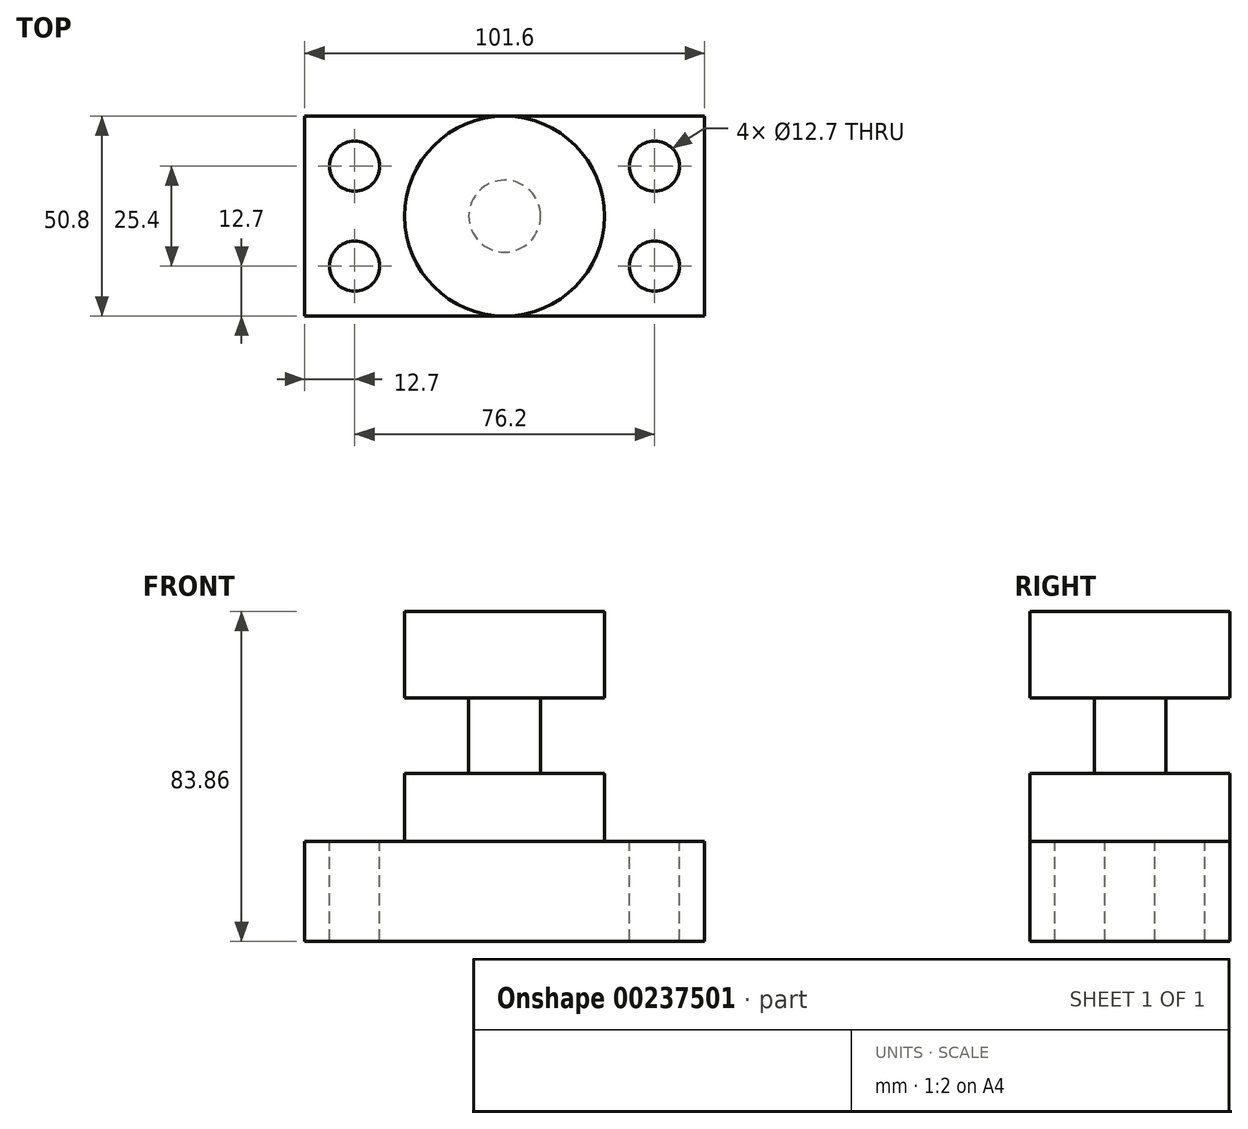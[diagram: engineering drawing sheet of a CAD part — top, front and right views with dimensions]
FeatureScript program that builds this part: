
annotation { "Feature Type Name" : "Feature", "Feature Type Description" : "" }
export const myFeature = defineFeature(function(context is Context, id is Id, definition is map)
    precondition{}
    {
        {
            var Q0;
            Q0=qCreatedBy(makeId("Top.planeOp"),FACE);
            var sketch = newSketch(context, id + "F0", { "sketchPlane" : qUnion([Q0])});
            skLineSegment(sketch, "E0.bottom", {"start": v(-50.8, 25.4) * mm, "end": v(50.8, 25.4) * mm});
            skLineSegment(sketch, "E0.top", {"start": v(-50.8, -25.4) * mm, "end": v(50.8, -25.4) * mm});
            skLineSegment(sketch, "E0.left", {"start": v(-50.8, 25.4) * mm, "end": v(-50.8, -25.4) * mm});
            skLineSegment(sketch, "E0.right", {"start": v(50.8, 25.4) * mm, "end": v(50.8, -25.4) * mm});
            skPoint(sketch, "E0.middle", {"position": v(0, 0) * mm});
            skSolve(sketch);
        }
        {
            var Q0;
            Q0=makeQuery(id+"F0.imprint","IMPRINT",FACE,{"disambiguationData":[TD([[makeQuery(id+"F0.imprint","IMPRINT",EDGE,{"derivedFrom":sQuery(id+"F0.wireOp",EDGE,"E0.bottom")}),-1.0]])]});
            extrude(context, id + "F1", {"entities" : qUnion([Q0]), "depth" : 25.4 * mm});
        }
        {
            var Q0;
            Q0=makeQuery(id+"F1.opExtrude","CAP_FACE",FACE,{"disambiguationData":[OSD([sQuery(id+"F0.wireOp",EDGE,"E0.bottom"),sQuery(id+"F0.wireOp",EDGE,"E0.top"),sQuery(id+"F0.wireOp",EDGE,"E0.left"),sQuery(id+"F0.wireOp",EDGE,"E0.right")])],"isStart":false});
            var sketch = newSketch(context, id + "F2", { "sketchPlane" : qUnion([Q0])});
            skCircle(sketch, "E1", {"center": v(-38.1, 12.7) * mm, "radius": 6.35 * mm});
            skCircle(sketch, "E2", {"center": v(-38.1, -12.7) * mm, "radius": 6.35 * mm});
            skCircle(sketch, "E3", {"center": v(38.1, 12.7) * mm, "radius": 6.35 * mm});
            skCircle(sketch, "E4", {"center": v(38.1, -12.7) * mm, "radius": 6.35 * mm});
            skSolve(sketch);
        }
        {
            var Q0;
            Q0=makeQuery(id+"F2.imprint","IMPRINT",FACE,{"disambiguationData":[TD([[makeQuery(id+"F2.imprint","IMPRINT",EDGE,{"derivedFrom":sQuery(id+"F2.wireOp",EDGE,"E1")}),1.0]])]});
            var Q1;
            Q1=makeQuery(id+"F2.imprint","IMPRINT",FACE,{"disambiguationData":[TD([[makeQuery(id+"F2.imprint","IMPRINT",EDGE,{"derivedFrom":sQuery(id+"F2.wireOp",EDGE,"E2")}),1.0]])]});
            var Q2;
            Q2=makeQuery(id+"F2.imprint","IMPRINT",FACE,{"disambiguationData":[TD([[makeQuery(id+"F2.imprint","IMPRINT",EDGE,{"derivedFrom":sQuery(id+"F2.wireOp",EDGE,"E4")}),1.0]])]});
            var Q3;
            Q3=makeQuery(id+"F2.imprint","IMPRINT",FACE,{"disambiguationData":[TD([[makeQuery(id+"F2.imprint","IMPRINT",EDGE,{"derivedFrom":sQuery(id+"F2.wireOp",EDGE,"E3")}),1.0]])]});
            extrude(context, id + "F3", {"entities" : qUnion([Q0, Q1, Q2, Q3]), "operationType" : NewBodyOperationType.REMOVE, "endBound" : BoundingType.THROUGH_ALL, "oppositeDirection" : true, "depth" : 50.8 * mm});
        }
        {
            var Q0;
            Q0=qCreatedBy(makeId("Front.planeOp"),FACE);
            var sketch = newSketch(context, id + "F4", { "sketchPlane" : qUnion([Q0])});
            skLineSegment(sketch, "E5.left", {"start": v(0, 25.44) * mm, "end": v(0, 83.86) * mm});
            skLineSegment(sketch, "E6.bottom", {"start": v(0, 83.86) * mm, "end": v(25.4, 83.86) * mm});
            skLineSegment(sketch, "E6.top", {"start": v(0, 25.44) * mm, "end": v(25.4, 25.44) * mm});
            skLineSegment(sketch, "E6.left", {"start": v(0, 83.86) * mm, "end": v(0, 25.44) * mm});
            skLineSegment(sketch, "E6.right", {"start": v(25.4, 83.86) * mm, "end": v(25.4, 25.44) * mm});
            skSolve(sketch);
        }
        {
            var Q0;
            Q0 = qSketchRegion(id + "F4", true);
            var Q1;
            Q1=sQuery(id+"F4.wireOp",EDGE,"E6.left");
            revolve(context, id + "F5", {"entities" : qUnion([Q0]), "axis" : qUnion([Q1]), "revolveType" : RevolveType.FULL});
        }
        {
            var Q0;
            Q0=qCreatedBy(makeId("Front.planeOp"),FACE);
            var sketch = newSketch(context, id + "F6", { "sketchPlane" : qUnion([Q0])});
            skLineSegment(sketch, "E7.bottom", {"start": v(-63.87, 61.82) * mm, "end": v(-9.12, 61.82) * mm});
            skLineSegment(sketch, "E7.top", {"start": v(-63.87, 42.66) * mm, "end": v(-9.12, 42.66) * mm});
            skLineSegment(sketch, "E7.left", {"start": v(-63.87, 61.82) * mm, "end": v(-63.87, 42.66) * mm});
            skLineSegment(sketch, "E7.right", {"start": v(-9.12, 61.82) * mm, "end": v(-9.12, 42.66) * mm});
            skSolve(sketch);
        }
        {
            var Q0;
            Q0=makeQuery(id+"F6.imprint","IMPRINT",FACE,{"disambiguationData":[TD([[makeQuery(id+"F6.imprint","IMPRINT",EDGE,{"derivedFrom":sQuery(id+"F6.wireOp",EDGE,"E7.bottom")}),-1.0]])]});
            var Q1;
            Q1=sQuery(id+"F4.wireOp",EDGE,"E6.left");
            revolve(context, id + "F7", {"operationType" : NewBodyOperationType.REMOVE, "entities" : qUnion([Q0]), "axis" : qUnion([Q1]), "revolveType" : RevolveType.FULL, "oppositeDirection" : true});
        }
    });
